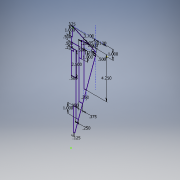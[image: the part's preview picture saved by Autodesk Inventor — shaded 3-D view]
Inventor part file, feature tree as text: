
AUTODESK INVENTOR PART (.ipt)
format: ipt  version: 2017 (Build 210142000, 142)  size: 123,904 bytes
history: native  units: in
note: dims shown in document units (in); Inventor stores cm internally (conversion verified against a paired STEP export)
features: sketch x1
ambient origin geometry x8: Origin, YZ Plane, XZ Plane, XY Plane, X Axis, Y Axis, Z Axis, Center Point
feature tree (1):
  sketch  "Sketch1"  dims[d0=1.13in d1=3.7in d2=0.125in d3=0.1718in d5=1.0in d6=1.0in d7=90.0deg d8=0.5in d9=15.0deg d12=1.25in d13=0.25in d16=0.5in d17=0.5in d18=0.5in d19=2.5in d20=0.5in d22=0.375in d23=0.25in d25=0.234in d26=15.0deg d27=0.125in d28=0.25in d29=1.0in d30=4.25in d31=0.25in d32=1.0in]
